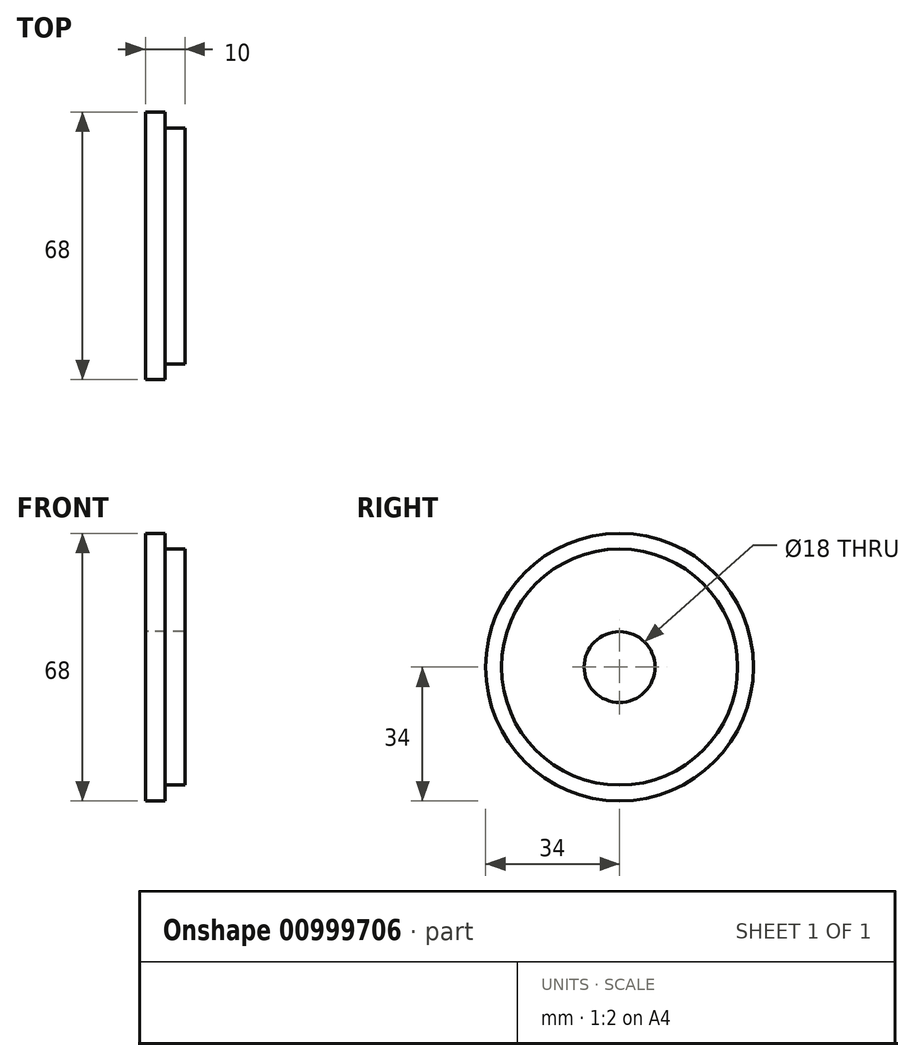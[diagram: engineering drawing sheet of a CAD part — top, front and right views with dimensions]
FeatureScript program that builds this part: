
annotation { "Feature Type Name" : "Feature", "Feature Type Description" : "" }
export const myFeature = defineFeature(function(context is Context, id is Id, definition is map)
    precondition{}
    {
        {
            var Q0;
            Q0=qCreatedBy(makeId("Front.planeOp"),FACE);
            var sketch = newSketch(context, id + "F0", { "sketchPlane" : qUnion([Q0])});
            skLineSegment(sketch, "E0", {"start": v(-78.75, 0) * mm, "end": v(96.55, 0) * mm, "construction": true});
            skLineSegment(sketch, "E1", {"start": v(-20.26, 9) * mm, "end": v(-20.26, 34) * mm});
            skLineSegment(sketch, "E2", {"start": v(-20.26, 34) * mm, "end": v(-15.26, 34) * mm});
            skLineSegment(sketch, "E3", {"start": v(-15.26, 34) * mm, "end": v(-15.26, 30) * mm});
            skLineSegment(sketch, "E4", {"start": v(-15.26, 30) * mm, "end": v(-10.26, 30) * mm});
            skLineSegment(sketch, "E5", {"start": v(-10.26, 30) * mm, "end": v(-10.26, 9) * mm});
            skLineSegment(sketch, "E6", {"start": v(-20.26, 9) * mm, "end": v(-10.26, 9) * mm});
            skPoint(sketch, "E7.orphan", {"position": v(-10.26, 0) * mm});
            skSolve(sketch);
        }
        {
            var Q0;
            Q0=makeQuery(id+"F0.imprint","IMPRINT",FACE,{"disambiguationData":[TD([[makeQuery(id+"F0.imprint","IMPRINT",EDGE,{"derivedFrom":sQuery(id+"F0.wireOp",EDGE,"E1")}),-1.0]])]});
            var Q1;
            Q1=sQuery(id+"F0.wireOp",EDGE,"E0");
            revolve(context, id + "F1", {"surfaceOperationType" : NewSurfaceOperationType.NEW, "entities" : qUnion([Q0]), "axis" : qUnion([Q1]), "revolveType" : RevolveType.FULL});
        }
    });
